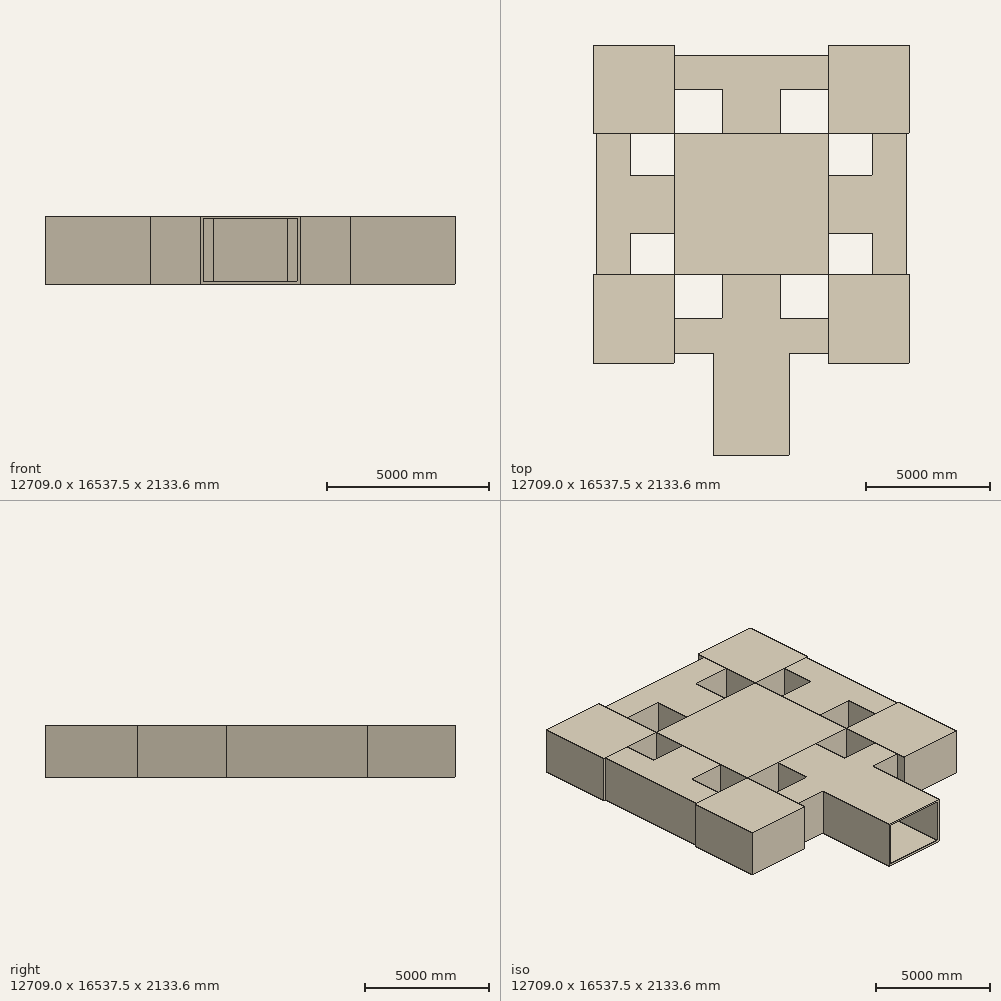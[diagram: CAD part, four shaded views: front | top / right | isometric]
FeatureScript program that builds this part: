
annotation { "Feature Type Name" : "Feature", "Feature Type Description" : "" }
export const myFeature = defineFeature(function(context is Context, id is Id, definition is map)
    precondition{}
    {
        {
            var Q0;
            Q0=qCreatedBy(makeId("Top.planeOp"),FACE);
            var sketch = newSketch(context, id + "F0", { "sketchPlane" : qUnion([Q0])});
            skLineSegment(sketch, "E0.top", {"start": v(13.99, 33.84) * mm, "end": v(36.85, 33.84) * mm});
            skLineSegment(sketch, "E0.right", {"start": v(36.85, 13.99) * mm, "end": v(36.85, 33.84) * mm});
            skLineSegment(sketch, "E1.bottom", {"start": v(36.85, 33.84) * mm, "end": v(56.25, 33.84) * mm});
            skLineSegment(sketch, "E1.top", {"start": v(36.85, 76.25) * mm, "end": v(75.65, 76.25) * mm});
            skLineSegment(sketch, "E1.left", {"start": v(36.85, 33.84) * mm, "end": v(36.85, 55.04) * mm});
            skLineSegment(sketch, "E1.right", {"start": v(75.65, 33.84) * mm, "end": v(75.65, 76.25) * mm});
            skLineSegment(sketch, "E2.bottom", {"start": v(36.85, 55.04) * mm, "end": v(13.99, 55.04) * mm});
            skLineSegment(sketch, "E2.top", {"start": v(36.85, 71.44) * mm, "end": v(0, 71.44) * mm});
            skLineSegment(sketch, "E3.trimOffspring", {"start": v(36.85, 71.44) * mm, "end": v(36.85, 76.25) * mm});
            skLineSegment(sketch, "E4.trimOffspring", {"start": v(56.25, 33.84) * mm, "end": v(58.05, 33.84) * mm});
            skLineSegment(sketch, "E5.right", {"start": v(13.99, 33.84) * mm, "end": v(13.99, 55.04) * mm});
            skLineSegment(sketch, "E6.left", {"start": v(36.85, 13.99) * mm, "end": v(58.05, 13.99) * mm});
            skLineSegment(sketch, "E7.top", {"start": v(74.45, 0) * mm, "end": v(74.45, 33.84) * mm});
            skLineSegment(sketch, "E8", {"start": v(58.05, 13.99) * mm, "end": v(58.05, 33.84) * mm});
            skLineSegment(sketch, "E9.MirrorCS", {"start": v(-36.85, 71.44) * mm, "end": v(-36.85, 76.25) * mm});
            skLineSegment(sketch, "E10.MirrorCS", {"start": v(-13.99, 33.84) * mm, "end": v(-36.85, 33.84) * mm});
            skLineSegment(sketch, "E11.MirrorCS", {"start": v(-36.85, 13.99) * mm, "end": v(-36.85, 33.84) * mm});
            skLineSegment(sketch, "E12.MirrorCS", {"start": v(-58.05, 13.99) * mm, "end": v(-58.05, 33.84) * mm});
            skLineSegment(sketch, "E13.MirrorCS", {"start": v(-74.45, 0) * mm, "end": v(-74.45, 33.84) * mm});
            skLineSegment(sketch, "E14.MirrorCS", {"start": v(-13.99, 33.84) * mm, "end": v(-13.99, 55.04) * mm});
            skLineSegment(sketch, "E15.MirrorCS", {"start": v(-56.25, 33.84) * mm, "end": v(-58.05, 33.84) * mm});
            skLineSegment(sketch, "E16.MirrorCS", {"start": v(-36.85, 33.84) * mm, "end": v(-56.25, 33.84) * mm});
            skLineSegment(sketch, "E17.MirrorCS", {"start": v(-36.85, 33.84) * mm, "end": v(-36.85, 55.04) * mm});
            skLineSegment(sketch, "E18.MirrorCS", {"start": v(-36.85, 76.25) * mm, "end": v(-75.65, 76.25) * mm});
            skLineSegment(sketch, "E19.MirrorCS", {"start": v(-36.85, 13.99) * mm, "end": v(-58.05, 13.99) * mm});
            skLineSegment(sketch, "E20.MirrorCS", {"start": v(-75.65, 33.84) * mm, "end": v(-75.65, 76.25) * mm});
            skLineSegment(sketch, "E21.MirrorCS", {"start": v(-36.85, 55.04) * mm, "end": v(-13.99, 55.04) * mm});
            skLineSegment(sketch, "E22.MirrorCS", {"start": v(-36.85, 71.44) * mm, "end": v(0, 71.44) * mm});
            skLineSegment(sketch, "E23.MirrorCS", {"start": v(-36.85, -71.44) * mm, "end": v(-36.85, -76.25) * mm});
            skLineSegment(sketch, "E24.MirrorCS", {"start": v(-36.85, -33.84) * mm, "end": v(-56.25, -33.84) * mm});
            skLineSegment(sketch, "E25.MirrorCS", {"start": v(36.85, -71.44) * mm, "end": v(36.85, -76.25) * mm});
            skLineSegment(sketch, "E26.MirrorCS", {"start": v(56.25, -33.84) * mm, "end": v(58.05, -33.84) * mm});
            skLineSegment(sketch, "E27.MirrorCS", {"start": v(-56.25, -33.84) * mm, "end": v(-58.05, -33.84) * mm});
            skLineSegment(sketch, "E28.MirrorCS", {"start": v(36.85, -71.44) * mm, "end": v(18.42, -71.44) * mm});
            skLineSegment(sketch, "E29.MirrorCS", {"start": v(36.85, -76.25) * mm, "end": v(75.65, -76.25) * mm});
            skLineSegment(sketch, "E30.MirrorCS", {"start": v(-13.99, -33.84) * mm, "end": v(-36.85, -33.84) * mm});
            skLineSegment(sketch, "E31.MirrorCS", {"start": v(-36.85, -13.99) * mm, "end": v(-36.85, -33.84) * mm});
            skLineSegment(sketch, "E32.MirrorCS", {"start": v(36.85, -55.04) * mm, "end": v(13.99, -55.04) * mm});
            skLineSegment(sketch, "E33.MirrorCS", {"start": v(-36.85, -13.99) * mm, "end": v(-58.05, -13.99) * mm});
            skLineSegment(sketch, "E34.MirrorCS", {"start": v(-36.85, -55.04) * mm, "end": v(-13.99, -55.04) * mm});
            skLineSegment(sketch, "E35.MirrorCS", {"start": v(-36.85, -33.84) * mm, "end": v(-36.85, -55.04) * mm});
            skLineSegment(sketch, "E36.MirrorCS", {"start": v(-36.85, -71.44) * mm, "end": v(-18.42, -71.44) * mm});
            skLineSegment(sketch, "E37.MirrorCS", {"start": v(36.85, -13.99) * mm, "end": v(36.85, -33.84) * mm});
            skLineSegment(sketch, "E38.MirrorCS", {"start": v(36.85, -13.99) * mm, "end": v(58.05, -13.99) * mm});
            skLineSegment(sketch, "E39.MirrorCS", {"start": v(36.85, -33.84) * mm, "end": v(56.25, -33.84) * mm});
            skLineSegment(sketch, "E40.MirrorCS", {"start": v(13.99, -33.84) * mm, "end": v(36.85, -33.84) * mm});
            skLineSegment(sketch, "E41.MirrorCS", {"start": v(58.05, -13.99) * mm, "end": v(58.05, -33.84) * mm});
            skLineSegment(sketch, "E42.MirrorCS", {"start": v(-74.45, 0) * mm, "end": v(-74.45, -33.84) * mm});
            skLineSegment(sketch, "E43.MirrorCS", {"start": v(-36.85, -76.25) * mm, "end": v(-75.65, -76.25) * mm});
            skLineSegment(sketch, "E44.MirrorCS", {"start": v(-58.05, -13.99) * mm, "end": v(-58.05, -33.84) * mm});
            skLineSegment(sketch, "E45.MirrorCS", {"start": v(13.99, -33.84) * mm, "end": v(13.99, -55.04) * mm});
            skLineSegment(sketch, "E46.MirrorCS", {"start": v(-13.99, -33.84) * mm, "end": v(-13.99, -55.04) * mm});
            skLineSegment(sketch, "E47.MirrorCS", {"start": v(75.65, -33.84) * mm, "end": v(75.65, -76.25) * mm});
            skLineSegment(sketch, "E48.MirrorCS", {"start": v(36.85, -33.84) * mm, "end": v(36.85, -55.04) * mm});
            skLineSegment(sketch, "E49.MirrorCS", {"start": v(74.45, 0) * mm, "end": v(74.45, -33.84) * mm});
            skLineSegment(sketch, "E50.MirrorCS", {"start": v(-75.65, -33.84) * mm, "end": v(-75.65, -76.25) * mm});
            skLineSegment(sketch, "E51.trimOffspring", {"start": v(-74.45, 33.84) * mm, "end": v(-75.65, 33.84) * mm});
            skLineSegment(sketch, "E52.trimOffspring", {"start": v(-74.45, -33.84) * mm, "end": v(-75.65, -33.84) * mm});
            skLineSegment(sketch, "E53.trimOffspring", {"start": v(74.45, -33.84) * mm, "end": v(75.65, -33.84) * mm});
            skLineSegment(sketch, "E54.trimOffspring", {"start": v(74.45, 33.84) * mm, "end": v(75.65, 33.84) * mm});
            skPoint(sketch, "E55.oppositeSnap0", {"position": v(18.42, -71.44) * mm});
            skLineSegment(sketch, "E55.top", {"start": v(-18.42, -120.63) * mm, "end": v(18.42, -120.63) * mm});
            skLineSegment(sketch, "E55.left", {"start": v(-18.42, -71.44) * mm, "end": v(-18.42, -120.63) * mm});
            skLineSegment(sketch, "E55.right", {"start": v(18.42, -71.44) * mm, "end": v(18.42, -120.63) * mm});
            skPoint(sketch, "E56.orphan", {"position": v(0, -71.44) * mm});
            skLineSegment(sketch, "E57", {"start": v(-13.99, 33.84) * mm, "end": v(13.99, 33.84) * mm});
            skLineSegment(sketch, "E58", {"start": v(36.85, 55.04) * mm, "end": v(36.85, 71.44) * mm});
            skLineSegment(sketch, "E59", {"start": v(-36.85, 71.44) * mm, "end": v(-36.85, 55.04) * mm});
            skLineSegment(sketch, "E60", {"start": v(13.99, -33.84) * mm, "end": v(-13.99, -33.84) * mm});
            skLineSegment(sketch, "E61", {"start": v(-36.85, -55.04) * mm, "end": v(-36.85, -71.44) * mm});
            skLineSegment(sketch, "E62", {"start": v(36.85, -71.44) * mm, "end": v(36.85, -55.04) * mm});
            skLineSegment(sketch, "E63", {"start": v(58.05, -33.83) * mm, "end": v(74.45, -33.83) * mm});
            skLineSegment(sketch, "E64", {"start": v(74.45, 33.84) * mm, "end": v(58.05, 33.84) * mm});
            skLineSegment(sketch, "E65", {"start": v(36.85, 13.99) * mm, "end": v(36.85, -13.99) * mm});
            skLineSegment(sketch, "E66", {"start": v(-36.85, 13.99) * mm, "end": v(-36.85, -13.99) * mm});
            skLineSegment(sketch, "E67", {"start": v(-58.05, -33.84) * mm, "end": v(-74.45, -33.84) * mm});
            skLineSegment(sketch, "E68", {"start": v(-74.45, 33.84) * mm, "end": v(-58.05, 33.84) * mm});
            skSolve(sketch);
        }
        {
            var Q0;
            Q0=makeQuery(id+"F0.imprint","IMPRINT",FACE,{"disambiguationData":[TD([[makeQuery(id+"F0.imprint","IMPRINT",EDGE,{"derivedFrom":sQuery(id+"F0.wireOp",EDGE,"E0.top")}),-1.0]])]});
            var Q1;
            Q1=makeQuery(id+"F0.imprint","IMPRINT",FACE,{"disambiguationData":[TD([[makeQuery(id+"F0.imprint","IMPRINT",EDGE,{"derivedFrom":sQuery(id+"F0.wireOp",EDGE,"E9.MirrorCS")}),1.0]])]});
            var Q2;
            Q2=makeQuery(id+"F0.imprint","IMPRINT",FACE,{"disambiguationData":[TD([[makeQuery(id+"F0.imprint","IMPRINT",EDGE,{"derivedFrom":sQuery(id+"F0.wireOp",EDGE,"E1.bottom")}),1.0]])]});
            var Q3;
            Q3=makeQuery(id+"F0.imprint","IMPRINT",FACE,{"disambiguationData":[TD([[makeQuery(id+"F0.imprint","IMPRINT",EDGE,{"derivedFrom":sQuery(id+"F0.wireOp",EDGE,"E25.MirrorCS")}),1.0]])]});
            var Q4;
            Q4=makeQuery(id+"F0.imprint","IMPRINT",FACE,{"disambiguationData":[TD([[makeQuery(id+"F0.imprint","IMPRINT",EDGE,{"derivedFrom":sQuery(id+"F0.wireOp",EDGE,"E23.MirrorCS")}),-1.0]])]});
            extrude(context, id + "F1", {"entities" : qUnion([Q0, Q1, Q2, Q3, Q4]), "depth" : 25.4 * mm, "offsetDistance" : 25.4 * mm});
        }
        {
            var Q0;
            Q0=makeQuery(id+"F0.imprint","IMPRINT",FACE,{"disambiguationData":[TD([[makeQuery(id+"F0.imprint","IMPRINT",EDGE,{"derivedFrom":sQuery(id+"F0.wireOp",EDGE,"E28.MirrorCS")}),-1.0]])]});
            var Q1;
            Q1=makeQuery(id+"F0.imprint","IMPRINT",FACE,{"disambiguationData":[TD([[makeQuery(id+"F0.imprint","IMPRINT",EDGE,{"derivedFrom":sQuery(id+"F0.wireOp",EDGE,"E6.left")}),-1.0]])]});
            var Q2;
            Q2=makeQuery(id+"F0.imprint","IMPRINT",FACE,{"disambiguationData":[TD([[makeQuery(id+"F0.imprint","IMPRINT",EDGE,{"derivedFrom":sQuery(id+"F0.wireOp",EDGE,"E2.bottom")}),-1.0]])]});
            var Q3;
            Q3=makeQuery(id+"F0.imprint","IMPRINT",FACE,{"disambiguationData":[TD([[makeQuery(id+"F0.imprint","IMPRINT",EDGE,{"derivedFrom":sQuery(id+"F0.wireOp",EDGE,"E12.MirrorCS")}),1.0]])]});
            extrude(context, id + "F2", {"entities" : qUnion([Q0, Q1, Q2, Q3]), "depth" : 25.4 * mm, "offsetDistance" : 25.4 * mm});
        }
        {
            var Q0;
            Q0=makeQuery(id+"F1.opExtrude","SWEPT_BODY",BODY,{"disambiguationData":[OSD([sQuery(id+"F0.wireOp",EDGE,"E25.MirrorCS"),sQuery(id+"F0.wireOp",EDGE,"E26.MirrorCS"),sQuery(id+"F0.wireOp",EDGE,"E29.MirrorCS"),sQuery(id+"F0.wireOp",EDGE,"E39.MirrorCS"),sQuery(id+"F0.wireOp",EDGE,"E41.MirrorCS"),sQuery(id+"F0.wireOp",EDGE,"E47.MirrorCS"),sQuery(id+"F0.wireOp",EDGE,"E48.MirrorCS"),sQuery(id+"F0.wireOp",EDGE,"E49.MirrorCS"),sQuery(id+"F0.wireOp",EDGE,"E53.trimOffspring"),sQuery(id+"F0.wireOp",EDGE,"E62"),sQuery(id+"F0.wireOp",EDGE,"E63")])]});
            var Q1;
            Q1=makeQuery(id+"F1.opExtrude","SWEPT_BODY",BODY,{"disambiguationData":[OSD([sQuery(id+"F0.wireOp",EDGE,"E23.MirrorCS"),sQuery(id+"F0.wireOp",EDGE,"E24.MirrorCS"),sQuery(id+"F0.wireOp",EDGE,"E27.MirrorCS"),sQuery(id+"F0.wireOp",EDGE,"E35.MirrorCS"),sQuery(id+"F0.wireOp",EDGE,"E43.MirrorCS"),sQuery(id+"F0.wireOp",EDGE,"E50.MirrorCS"),sQuery(id+"F0.wireOp",EDGE,"E52.trimOffspring"),sQuery(id+"F0.wireOp",EDGE,"E61"),sQuery(id+"F0.wireOp",EDGE,"E67")])]});
            var Q2;
            Q2=makeQuery(id+"F1.opExtrude","SWEPT_BODY",BODY,{"disambiguationData":[OSD([sQuery(id+"F0.wireOp",EDGE,"E1.bottom"),sQuery(id+"F0.wireOp",EDGE,"E1.top"),sQuery(id+"F0.wireOp",EDGE,"E1.left"),sQuery(id+"F0.wireOp",EDGE,"E1.right"),sQuery(id+"F0.wireOp",EDGE,"E3.trimOffspring"),sQuery(id+"F0.wireOp",EDGE,"E4.trimOffspring"),sQuery(id+"F0.wireOp",EDGE,"E54.trimOffspring"),sQuery(id+"F0.wireOp",EDGE,"E58"),sQuery(id+"F0.wireOp",EDGE,"E64")])]});
            var Q3;
            Q3=makeQuery(id+"F1.opExtrude","SWEPT_BODY",BODY,{"disambiguationData":[OSD([sQuery(id+"F0.wireOp",EDGE,"E9.MirrorCS"),sQuery(id+"F0.wireOp",EDGE,"E15.MirrorCS"),sQuery(id+"F0.wireOp",EDGE,"E16.MirrorCS"),sQuery(id+"F0.wireOp",EDGE,"E17.MirrorCS"),sQuery(id+"F0.wireOp",EDGE,"E18.MirrorCS"),sQuery(id+"F0.wireOp",EDGE,"E20.MirrorCS"),sQuery(id+"F0.wireOp",EDGE,"E51.trimOffspring"),sQuery(id+"F0.wireOp",EDGE,"E59"),sQuery(id+"F0.wireOp",EDGE,"E68")])]});
            var Q4;
            Q4=makeQuery(id+"F1.opExtrude","SWEPT_BODY",BODY,{"disambiguationData":[OSD([sQuery(id+"F0.wireOp",EDGE,"E0.top"),sQuery(id+"F0.wireOp",EDGE,"E0.right"),sQuery(id+"F0.wireOp",EDGE,"E10.MirrorCS"),sQuery(id+"F0.wireOp",EDGE,"E11.MirrorCS"),sQuery(id+"F0.wireOp",EDGE,"E30.MirrorCS"),sQuery(id+"F0.wireOp",EDGE,"E31.MirrorCS"),sQuery(id+"F0.wireOp",EDGE,"E37.MirrorCS"),sQuery(id+"F0.wireOp",EDGE,"E40.MirrorCS"),sQuery(id+"F0.wireOp",EDGE,"E57"),sQuery(id+"F0.wireOp",EDGE,"E60"),sQuery(id+"F0.wireOp",EDGE,"E65"),sQuery(id+"F0.wireOp",EDGE,"E66")])]});
            var Q5;
            Q5=makeQuery(id+"F2.opExtrude","SWEPT_BODY",BODY,{"disambiguationData":[OSD([sQuery(id+"F0.wireOp",EDGE,"E2.bottom"),sQuery(id+"F0.wireOp",EDGE,"E2.top"),sQuery(id+"F0.wireOp",EDGE,"E5.right"),sQuery(id+"F0.wireOp",EDGE,"E14.MirrorCS"),sQuery(id+"F0.wireOp",EDGE,"E21.MirrorCS"),sQuery(id+"F0.wireOp",EDGE,"E22.MirrorCS"),sQuery(id+"F0.wireOp",EDGE,"E57"),sQuery(id+"F0.wireOp",EDGE,"E58"),sQuery(id+"F0.wireOp",EDGE,"E59")])]});
            var Q6;
            Q6=makeQuery(id+"F2.opExtrude","SWEPT_BODY",BODY,{"disambiguationData":[OSD([sQuery(id+"F0.wireOp",EDGE,"E6.left"),sQuery(id+"F0.wireOp",EDGE,"E7.top"),sQuery(id+"F0.wireOp",EDGE,"E8"),sQuery(id+"F0.wireOp",EDGE,"E38.MirrorCS"),sQuery(id+"F0.wireOp",EDGE,"E41.MirrorCS"),sQuery(id+"F0.wireOp",EDGE,"E49.MirrorCS"),sQuery(id+"F0.wireOp",EDGE,"E63"),sQuery(id+"F0.wireOp",EDGE,"E64"),sQuery(id+"F0.wireOp",EDGE,"E65")])]});
            var Q7;
            Q7=makeQuery(id+"F2.opExtrude","SWEPT_BODY",BODY,{"disambiguationData":[OSD([sQuery(id+"F0.wireOp",EDGE,"E12.MirrorCS"),sQuery(id+"F0.wireOp",EDGE,"E13.MirrorCS"),sQuery(id+"F0.wireOp",EDGE,"E19.MirrorCS"),sQuery(id+"F0.wireOp",EDGE,"E33.MirrorCS"),sQuery(id+"F0.wireOp",EDGE,"E42.MirrorCS"),sQuery(id+"F0.wireOp",EDGE,"E44.MirrorCS"),sQuery(id+"F0.wireOp",EDGE,"E66"),sQuery(id+"F0.wireOp",EDGE,"E67"),sQuery(id+"F0.wireOp",EDGE,"E68")])]});
            var Q8;
            Q8=makeQuery(id+"F2.opExtrude","SWEPT_BODY",BODY,{"disambiguationData":[OSD([sQuery(id+"F0.wireOp",EDGE,"E28.MirrorCS"),sQuery(id+"F0.wireOp",EDGE,"E32.MirrorCS"),sQuery(id+"F0.wireOp",EDGE,"E34.MirrorCS"),sQuery(id+"F0.wireOp",EDGE,"E36.MirrorCS"),sQuery(id+"F0.wireOp",EDGE,"E45.MirrorCS"),sQuery(id+"F0.wireOp",EDGE,"E46.MirrorCS"),sQuery(id+"F0.wireOp",EDGE,"E55.top"),sQuery(id+"F0.wireOp",EDGE,"E55.left"),sQuery(id+"F0.wireOp",EDGE,"E55.right"),sQuery(id+"F0.wireOp",EDGE,"E60"),sQuery(id+"F0.wireOp",EDGE,"E61"),sQuery(id+"F0.wireOp",EDGE,"E62")])]});
            var Q9;
            Q9=qCreatedBy(makeId("Origin.pointOp"),VERTEX);
            transform(context, id + "F3", {"entities" : qUnion([Q0, Q1, Q2, Q3, Q4, Q5, Q6, Q7, Q8]), "transformType" : TransformType.SCALE_UNIFORMLY, "scale" : 84, "scalePoint" : qUnion([Q9]), "makeCopy" : false});
        }
        {
            var Q0;
            Q0=makeQuery(id+"F1.opExtrude","CAP_FACE",FACE,{"disambiguationData":[OSD([sQuery(id+"F0.wireOp",EDGE,"E25.MirrorCS"),sQuery(id+"F0.wireOp",EDGE,"E26.MirrorCS"),sQuery(id+"F0.wireOp",EDGE,"E29.MirrorCS"),sQuery(id+"F0.wireOp",EDGE,"E39.MirrorCS"),sQuery(id+"F0.wireOp",EDGE,"E41.MirrorCS"),sQuery(id+"F0.wireOp",EDGE,"E47.MirrorCS"),sQuery(id+"F0.wireOp",EDGE,"E48.MirrorCS"),sQuery(id+"F0.wireOp",EDGE,"E49.MirrorCS"),sQuery(id+"F0.wireOp",EDGE,"E53.trimOffspring"),sQuery(id+"F0.wireOp",EDGE,"E62"),sQuery(id+"F0.wireOp",EDGE,"E63")])],"isStart":true});
            var Q1;
            Q1=makeQuery(id+"F1.opExtrude","CAP_FACE",FACE,{"disambiguationData":[OSD([sQuery(id+"F0.wireOp",EDGE,"E25.MirrorCS"),sQuery(id+"F0.wireOp",EDGE,"E26.MirrorCS"),sQuery(id+"F0.wireOp",EDGE,"E29.MirrorCS"),sQuery(id+"F0.wireOp",EDGE,"E39.MirrorCS"),sQuery(id+"F0.wireOp",EDGE,"E41.MirrorCS"),sQuery(id+"F0.wireOp",EDGE,"E47.MirrorCS"),sQuery(id+"F0.wireOp",EDGE,"E48.MirrorCS"),sQuery(id+"F0.wireOp",EDGE,"E49.MirrorCS"),sQuery(id+"F0.wireOp",EDGE,"E53.trimOffspring"),sQuery(id+"F0.wireOp",EDGE,"E62"),sQuery(id+"F0.wireOp",EDGE,"E63")])],"isStart":false});
            var Q2;
            Q2=makeQuery(id+"F1.opExtrude","SWEPT_FACE",FACE,{"disambiguationData":[OSD([sQuery(id+"F0.wireOp",EDGE,"E53.trimOffspring")])]});
            var Q3;
            Q3=makeQuery(id+"F1.opExtrude","SWEPT_FACE",FACE,{"disambiguationData":[OSD([sQuery(id+"F0.wireOp",EDGE,"E47.MirrorCS")])]});
            var Q4;
            Q4=makeQuery(id+"F1.opExtrude","SWEPT_FACE",FACE,{"disambiguationData":[OSD([sQuery(id+"F0.wireOp",EDGE,"E26.MirrorCS"),sQuery(id+"F0.wireOp",EDGE,"E39.MirrorCS")])]});
            var Q5;
            Q5=makeQuery(id+"F1.opExtrude","SWEPT_FACE",FACE,{"disambiguationData":[OSD([sQuery(id+"F0.wireOp",EDGE,"E29.MirrorCS")])]});
            var Q6;
            Q6=makeQuery(id+"F1.opExtrude","SWEPT_FACE",FACE,{"disambiguationData":[OSD([sQuery(id+"F0.wireOp",EDGE,"E50.MirrorCS")])]});
            var Q7;
            Q7=makeQuery(id+"F1.opExtrude","CAP_FACE",FACE,{"disambiguationData":[OSD([sQuery(id+"F0.wireOp",EDGE,"E23.MirrorCS"),sQuery(id+"F0.wireOp",EDGE,"E24.MirrorCS"),sQuery(id+"F0.wireOp",EDGE,"E27.MirrorCS"),sQuery(id+"F0.wireOp",EDGE,"E35.MirrorCS"),sQuery(id+"F0.wireOp",EDGE,"E43.MirrorCS"),sQuery(id+"F0.wireOp",EDGE,"E50.MirrorCS"),sQuery(id+"F0.wireOp",EDGE,"E52.trimOffspring"),sQuery(id+"F0.wireOp",EDGE,"E61"),sQuery(id+"F0.wireOp",EDGE,"E67")])],"isStart":false});
            var Q8;
            Q8=makeQuery(id+"F1.opExtrude","SWEPT_FACE",FACE,{"disambiguationData":[OSD([sQuery(id+"F0.wireOp",EDGE,"E23.MirrorCS"),sQuery(id+"F0.wireOp",EDGE,"E35.MirrorCS"),sQuery(id+"F0.wireOp",EDGE,"E61")])]});
            var Q9;
            Q9=makeQuery(id+"F1.opExtrude","SWEPT_FACE",FACE,{"disambiguationData":[OSD([sQuery(id+"F0.wireOp",EDGE,"E24.MirrorCS"),sQuery(id+"F0.wireOp",EDGE,"E27.MirrorCS"),sQuery(id+"F0.wireOp",EDGE,"E52.trimOffspring"),sQuery(id+"F0.wireOp",EDGE,"E67")])]});
            var Q10;
            Q10=makeQuery(id+"F1.opExtrude","SWEPT_FACE",FACE,{"disambiguationData":[OSD([sQuery(id+"F0.wireOp",EDGE,"E43.MirrorCS")])]});
            var Q11;
            Q11=makeQuery(id+"F1.opExtrude","SWEPT_FACE",FACE,{"disambiguationData":[OSD([sQuery(id+"F0.wireOp",EDGE,"E1.right")])]});
            var Q12;
            Q12=makeQuery(id+"F1.opExtrude","CAP_FACE",FACE,{"disambiguationData":[OSD([sQuery(id+"F0.wireOp",EDGE,"E1.bottom"),sQuery(id+"F0.wireOp",EDGE,"E1.top"),sQuery(id+"F0.wireOp",EDGE,"E1.left"),sQuery(id+"F0.wireOp",EDGE,"E1.right"),sQuery(id+"F0.wireOp",EDGE,"E3.trimOffspring"),sQuery(id+"F0.wireOp",EDGE,"E4.trimOffspring"),sQuery(id+"F0.wireOp",EDGE,"E54.trimOffspring"),sQuery(id+"F0.wireOp",EDGE,"E58"),sQuery(id+"F0.wireOp",EDGE,"E64")])],"isStart":false});
            var Q13;
            Q13=makeQuery(id+"F1.opExtrude","SWEPT_FACE",FACE,{"disambiguationData":[OSD([sQuery(id+"F0.wireOp",EDGE,"E1.left"),sQuery(id+"F0.wireOp",EDGE,"E3.trimOffspring"),sQuery(id+"F0.wireOp",EDGE,"E58")])]});
            var Q14;
            Q14=makeQuery(id+"F1.opExtrude","SWEPT_FACE",FACE,{"disambiguationData":[OSD([sQuery(id+"F0.wireOp",EDGE,"E1.bottom"),sQuery(id+"F0.wireOp",EDGE,"E4.trimOffspring"),sQuery(id+"F0.wireOp",EDGE,"E54.trimOffspring"),sQuery(id+"F0.wireOp",EDGE,"E64")])]});
            var Q15;
            Q15=makeQuery(id+"F1.opExtrude","CAP_FACE",FACE,{"disambiguationData":[OSD([sQuery(id+"F0.wireOp",EDGE,"E9.MirrorCS"),sQuery(id+"F0.wireOp",EDGE,"E15.MirrorCS"),sQuery(id+"F0.wireOp",EDGE,"E16.MirrorCS"),sQuery(id+"F0.wireOp",EDGE,"E17.MirrorCS"),sQuery(id+"F0.wireOp",EDGE,"E18.MirrorCS"),sQuery(id+"F0.wireOp",EDGE,"E20.MirrorCS"),sQuery(id+"F0.wireOp",EDGE,"E51.trimOffspring"),sQuery(id+"F0.wireOp",EDGE,"E59"),sQuery(id+"F0.wireOp",EDGE,"E68")])],"isStart":false});
            var Q16;
            Q16=makeQuery(id+"F1.opExtrude","SWEPT_FACE",FACE,{"disambiguationData":[OSD([sQuery(id+"F0.wireOp",EDGE,"E9.MirrorCS"),sQuery(id+"F0.wireOp",EDGE,"E17.MirrorCS"),sQuery(id+"F0.wireOp",EDGE,"E59")])]});
            var Q17;
            Q17=makeQuery(id+"F1.opExtrude","SWEPT_FACE",FACE,{"disambiguationData":[OSD([sQuery(id+"F0.wireOp",EDGE,"E15.MirrorCS"),sQuery(id+"F0.wireOp",EDGE,"E16.MirrorCS"),sQuery(id+"F0.wireOp",EDGE,"E51.trimOffspring"),sQuery(id+"F0.wireOp",EDGE,"E68")])]});
            var Q18;
            Q18=makeQuery(id+"F1.opExtrude","SWEPT_FACE",FACE,{"disambiguationData":[OSD([sQuery(id+"F0.wireOp",EDGE,"E20.MirrorCS")])]});
            var Q19;
            Q19=makeQuery(id+"F1.opExtrude","SWEPT_FACE",FACE,{"disambiguationData":[OSD([sQuery(id+"F0.wireOp",EDGE,"E18.MirrorCS")])]});
            var Q20;
            Q20=makeQuery(id+"F1.opExtrude","CAP_FACE",FACE,{"disambiguationData":[OSD([sQuery(id+"F0.wireOp",EDGE,"E0.top"),sQuery(id+"F0.wireOp",EDGE,"E0.right"),sQuery(id+"F0.wireOp",EDGE,"E10.MirrorCS"),sQuery(id+"F0.wireOp",EDGE,"E11.MirrorCS"),sQuery(id+"F0.wireOp",EDGE,"E30.MirrorCS"),sQuery(id+"F0.wireOp",EDGE,"E31.MirrorCS"),sQuery(id+"F0.wireOp",EDGE,"E37.MirrorCS"),sQuery(id+"F0.wireOp",EDGE,"E40.MirrorCS"),sQuery(id+"F0.wireOp",EDGE,"E57"),sQuery(id+"F0.wireOp",EDGE,"E60"),sQuery(id+"F0.wireOp",EDGE,"E65"),sQuery(id+"F0.wireOp",EDGE,"E66")])],"isStart":false});
            var Q21;
            Q21=makeQuery(id+"F1.opExtrude","SWEPT_FACE",FACE,{"disambiguationData":[OSD([sQuery(id+"F0.wireOp",EDGE,"E11.MirrorCS"),sQuery(id+"F0.wireOp",EDGE,"E31.MirrorCS"),sQuery(id+"F0.wireOp",EDGE,"E66")])]});
            var Q22;
            Q22=makeQuery(id+"F1.opExtrude","SWEPT_FACE",FACE,{"disambiguationData":[OSD([sQuery(id+"F0.wireOp",EDGE,"E0.top"),sQuery(id+"F0.wireOp",EDGE,"E10.MirrorCS"),sQuery(id+"F0.wireOp",EDGE,"E57")])]});
            var Q23;
            Q23=makeQuery(id+"F1.opExtrude","SWEPT_FACE",FACE,{"disambiguationData":[OSD([sQuery(id+"F0.wireOp",EDGE,"E30.MirrorCS"),sQuery(id+"F0.wireOp",EDGE,"E40.MirrorCS"),sQuery(id+"F0.wireOp",EDGE,"E60")])]});
            var Q24;
            Q24=makeQuery(id+"F1.opExtrude","SWEPT_FACE",FACE,{"disambiguationData":[OSD([sQuery(id+"F0.wireOp",EDGE,"E0.right"),sQuery(id+"F0.wireOp",EDGE,"E37.MirrorCS"),sQuery(id+"F0.wireOp",EDGE,"E65")])]});
            var Q25;
            Q25=makeQuery(id+"F2.opExtrude","SWEPT_FACE",FACE,{"disambiguationData":[OSD([sQuery(id+"F0.wireOp",EDGE,"E14.MirrorCS")])]});
            var Q26;
            Q26=makeQuery(id+"F2.opExtrude","SWEPT_FACE",FACE,{"disambiguationData":[OSD([sQuery(id+"F0.wireOp",EDGE,"E21.MirrorCS")])]});
            var Q27;
            Q27=makeQuery(id+"F2.opExtrude","SWEPT_FACE",FACE,{"disambiguationData":[OSD([sQuery(id+"F0.wireOp",EDGE,"E5.right")])]});
            var Q28;
            Q28=makeQuery(id+"F2.opExtrude","CAP_FACE",FACE,{"disambiguationData":[OSD([sQuery(id+"F0.wireOp",EDGE,"E2.bottom"),sQuery(id+"F0.wireOp",EDGE,"E2.top"),sQuery(id+"F0.wireOp",EDGE,"E5.right"),sQuery(id+"F0.wireOp",EDGE,"E14.MirrorCS"),sQuery(id+"F0.wireOp",EDGE,"E21.MirrorCS"),sQuery(id+"F0.wireOp",EDGE,"E22.MirrorCS"),sQuery(id+"F0.wireOp",EDGE,"E57"),sQuery(id+"F0.wireOp",EDGE,"E58"),sQuery(id+"F0.wireOp",EDGE,"E59")])],"isStart":false});
            var Q29;
            Q29=makeQuery(id+"F2.opExtrude","SWEPT_FACE",FACE,{"disambiguationData":[OSD([sQuery(id+"F0.wireOp",EDGE,"E2.bottom")])]});
            var Q30;
            Q30=makeQuery(id+"F2.opExtrude","CAP_FACE",FACE,{"disambiguationData":[OSD([sQuery(id+"F0.wireOp",EDGE,"E6.left"),sQuery(id+"F0.wireOp",EDGE,"E7.top"),sQuery(id+"F0.wireOp",EDGE,"E8"),sQuery(id+"F0.wireOp",EDGE,"E38.MirrorCS"),sQuery(id+"F0.wireOp",EDGE,"E41.MirrorCS"),sQuery(id+"F0.wireOp",EDGE,"E49.MirrorCS"),sQuery(id+"F0.wireOp",EDGE,"E63"),sQuery(id+"F0.wireOp",EDGE,"E64"),sQuery(id+"F0.wireOp",EDGE,"E65")])],"isStart":true});
            var Q31;
            Q31=makeQuery(id+"F2.opExtrude","SWEPT_FACE",FACE,{"disambiguationData":[OSD([sQuery(id+"F0.wireOp",EDGE,"E41.MirrorCS")])]});
            var Q32;
            Q32=makeQuery(id+"F2.opExtrude","SWEPT_FACE",FACE,{"disambiguationData":[OSD([sQuery(id+"F0.wireOp",EDGE,"E38.MirrorCS")])]});
            var Q33;
            Q33=makeQuery(id+"F2.opExtrude","CAP_FACE",FACE,{"disambiguationData":[OSD([sQuery(id+"F0.wireOp",EDGE,"E6.left"),sQuery(id+"F0.wireOp",EDGE,"E7.top"),sQuery(id+"F0.wireOp",EDGE,"E8"),sQuery(id+"F0.wireOp",EDGE,"E38.MirrorCS"),sQuery(id+"F0.wireOp",EDGE,"E41.MirrorCS"),sQuery(id+"F0.wireOp",EDGE,"E49.MirrorCS"),sQuery(id+"F0.wireOp",EDGE,"E63"),sQuery(id+"F0.wireOp",EDGE,"E64"),sQuery(id+"F0.wireOp",EDGE,"E65")])],"isStart":false});
            var Q34;
            Q34=makeQuery(id+"F2.opExtrude","SWEPT_FACE",FACE,{"disambiguationData":[OSD([sQuery(id+"F0.wireOp",EDGE,"E8")])]});
            var Q35;
            Q35=makeQuery(id+"F2.opExtrude","SWEPT_FACE",FACE,{"disambiguationData":[OSD([sQuery(id+"F0.wireOp",EDGE,"E65")])]});
            var Q36;
            Q36=makeQuery(id+"F2.opExtrude","SWEPT_FACE",FACE,{"disambiguationData":[OSD([sQuery(id+"F0.wireOp",EDGE,"E6.left")])]});
            var Q37;
            Q37=makeQuery(id+"F2.opExtrude","SWEPT_FACE",FACE,{"disambiguationData":[OSD([sQuery(id+"F0.wireOp",EDGE,"E7.top"),sQuery(id+"F0.wireOp",EDGE,"E49.MirrorCS")])]});
            var Q38;
            Q38=makeQuery(id+"F2.opExtrude","SWEPT_FACE",FACE,{"disambiguationData":[OSD([sQuery(id+"F0.wireOp",EDGE,"E13.MirrorCS"),sQuery(id+"F0.wireOp",EDGE,"E42.MirrorCS")])]});
            var Q39;
            Q39=makeQuery(id+"F2.opExtrude","SWEPT_FACE",FACE,{"disambiguationData":[OSD([sQuery(id+"F0.wireOp",EDGE,"E33.MirrorCS")])]});
            var Q40;
            Q40=makeQuery(id+"F2.opExtrude","SWEPT_FACE",FACE,{"disambiguationData":[OSD([sQuery(id+"F0.wireOp",EDGE,"E12.MirrorCS")])]});
            var Q41;
            Q41=makeQuery(id+"F2.opExtrude","SWEPT_FACE",FACE,{"disambiguationData":[OSD([sQuery(id+"F0.wireOp",EDGE,"E44.MirrorCS")])]});
            var Q42;
            Q42=makeQuery(id+"F2.opExtrude","SWEPT_FACE",FACE,{"disambiguationData":[OSD([sQuery(id+"F0.wireOp",EDGE,"E19.MirrorCS")])]});
            var Q43;
            Q43=makeQuery(id+"F2.opExtrude","CAP_FACE",FACE,{"disambiguationData":[OSD([sQuery(id+"F0.wireOp",EDGE,"E12.MirrorCS"),sQuery(id+"F0.wireOp",EDGE,"E13.MirrorCS"),sQuery(id+"F0.wireOp",EDGE,"E19.MirrorCS"),sQuery(id+"F0.wireOp",EDGE,"E33.MirrorCS"),sQuery(id+"F0.wireOp",EDGE,"E42.MirrorCS"),sQuery(id+"F0.wireOp",EDGE,"E44.MirrorCS"),sQuery(id+"F0.wireOp",EDGE,"E66"),sQuery(id+"F0.wireOp",EDGE,"E67"),sQuery(id+"F0.wireOp",EDGE,"E68")])],"isStart":false});
            var Q44;
            Q44=makeQuery(id+"F2.opExtrude","SWEPT_FACE",FACE,{"disambiguationData":[OSD([sQuery(id+"F0.wireOp",EDGE,"E36.MirrorCS")])]});
            var Q45;
            Q45=makeQuery(id+"F2.opExtrude","SWEPT_FACE",FACE,{"disambiguationData":[OSD([sQuery(id+"F0.wireOp",EDGE,"E61")])]});
            var Q46;
            Q46=makeQuery(id+"F2.opExtrude","SWEPT_FACE",FACE,{"disambiguationData":[OSD([sQuery(id+"F0.wireOp",EDGE,"E55.top")])]});
            var Q47;
            Q47=makeQuery(id+"F2.opExtrude","SWEPT_FACE",FACE,{"disambiguationData":[OSD([sQuery(id+"F0.wireOp",EDGE,"E55.left")])]});
            var Q48;
            Q48=makeQuery(id+"F2.opExtrude","SWEPT_FACE",FACE,{"disambiguationData":[OSD([sQuery(id+"F0.wireOp",EDGE,"E55.right")])]});
            var Q49;
            Q49=makeQuery(id+"F2.opExtrude","SWEPT_FACE",FACE,{"disambiguationData":[OSD([sQuery(id+"F0.wireOp",EDGE,"E28.MirrorCS")])]});
            var Q50;
            Q50=makeQuery(id+"F2.opExtrude","SWEPT_FACE",FACE,{"disambiguationData":[OSD([sQuery(id+"F0.wireOp",EDGE,"E34.MirrorCS")])]});
            var Q51;
            Q51=makeQuery(id+"F2.opExtrude","SWEPT_FACE",FACE,{"disambiguationData":[OSD([sQuery(id+"F0.wireOp",EDGE,"E32.MirrorCS")])]});
            var Q52;
            Q52=makeQuery(id+"F2.opExtrude","CAP_FACE",FACE,{"disambiguationData":[OSD([sQuery(id+"F0.wireOp",EDGE,"E28.MirrorCS"),sQuery(id+"F0.wireOp",EDGE,"E32.MirrorCS"),sQuery(id+"F0.wireOp",EDGE,"E34.MirrorCS"),sQuery(id+"F0.wireOp",EDGE,"E36.MirrorCS"),sQuery(id+"F0.wireOp",EDGE,"E45.MirrorCS"),sQuery(id+"F0.wireOp",EDGE,"E46.MirrorCS"),sQuery(id+"F0.wireOp",EDGE,"E55.top"),sQuery(id+"F0.wireOp",EDGE,"E55.left"),sQuery(id+"F0.wireOp",EDGE,"E55.right"),sQuery(id+"F0.wireOp",EDGE,"E60"),sQuery(id+"F0.wireOp",EDGE,"E61"),sQuery(id+"F0.wireOp",EDGE,"E62")])],"isStart":false});
            var Q53;
            Q53=makeQuery(id+"F2.opExtrude","SWEPT_FACE",FACE,{"disambiguationData":[OSD([sQuery(id+"F0.wireOp",EDGE,"E46.MirrorCS")])]});
            var Q54;
            Q54=makeQuery(id+"F1.opExtrude","SWEPT_FACE",FACE,{"disambiguationData":[OSD([sQuery(id+"F0.wireOp",EDGE,"E25.MirrorCS"),sQuery(id+"F0.wireOp",EDGE,"E48.MirrorCS"),sQuery(id+"F0.wireOp",EDGE,"E62")])]});
            var Q55;
            Q55=makeQuery(id+"F1.opExtrude","SWEPT_FACE",FACE,{"disambiguationData":[OSD([sQuery(id+"F0.wireOp",EDGE,"E63")])]});
            var Q56;
            Q56=makeQuery(id+"F1.opExtrude","SWEPT_FACE",FACE,{"disambiguationData":[OSD([sQuery(id+"F0.wireOp",EDGE,"E41.MirrorCS")])]});
            var Q57;
            Q57=makeQuery(id+"F1.opExtrude","CAP_FACE",FACE,{"disambiguationData":[OSD([sQuery(id+"F0.wireOp",EDGE,"E23.MirrorCS"),sQuery(id+"F0.wireOp",EDGE,"E24.MirrorCS"),sQuery(id+"F0.wireOp",EDGE,"E27.MirrorCS"),sQuery(id+"F0.wireOp",EDGE,"E35.MirrorCS"),sQuery(id+"F0.wireOp",EDGE,"E43.MirrorCS"),sQuery(id+"F0.wireOp",EDGE,"E50.MirrorCS"),sQuery(id+"F0.wireOp",EDGE,"E52.trimOffspring"),sQuery(id+"F0.wireOp",EDGE,"E61"),sQuery(id+"F0.wireOp",EDGE,"E67")])],"isStart":true});
            var Q58;
            Q58=makeQuery(id+"F1.opExtrude","CAP_FACE",FACE,{"disambiguationData":[OSD([sQuery(id+"F0.wireOp",EDGE,"E1.bottom"),sQuery(id+"F0.wireOp",EDGE,"E1.top"),sQuery(id+"F0.wireOp",EDGE,"E1.left"),sQuery(id+"F0.wireOp",EDGE,"E1.right"),sQuery(id+"F0.wireOp",EDGE,"E3.trimOffspring"),sQuery(id+"F0.wireOp",EDGE,"E4.trimOffspring"),sQuery(id+"F0.wireOp",EDGE,"E54.trimOffspring"),sQuery(id+"F0.wireOp",EDGE,"E58"),sQuery(id+"F0.wireOp",EDGE,"E64")])],"isStart":true});
            var Q59;
            Q59=makeQuery(id+"F1.opExtrude","SWEPT_FACE",FACE,{"disambiguationData":[OSD([sQuery(id+"F0.wireOp",EDGE,"E1.top")])]});
            var Q60;
            Q60=makeQuery(id+"F1.opExtrude","CAP_FACE",FACE,{"disambiguationData":[OSD([sQuery(id+"F0.wireOp",EDGE,"E9.MirrorCS"),sQuery(id+"F0.wireOp",EDGE,"E15.MirrorCS"),sQuery(id+"F0.wireOp",EDGE,"E16.MirrorCS"),sQuery(id+"F0.wireOp",EDGE,"E17.MirrorCS"),sQuery(id+"F0.wireOp",EDGE,"E18.MirrorCS"),sQuery(id+"F0.wireOp",EDGE,"E20.MirrorCS"),sQuery(id+"F0.wireOp",EDGE,"E51.trimOffspring"),sQuery(id+"F0.wireOp",EDGE,"E59"),sQuery(id+"F0.wireOp",EDGE,"E68")])],"isStart":true});
            var Q61;
            Q61=makeQuery(id+"F1.opExtrude","CAP_FACE",FACE,{"disambiguationData":[OSD([sQuery(id+"F0.wireOp",EDGE,"E0.top"),sQuery(id+"F0.wireOp",EDGE,"E0.right"),sQuery(id+"F0.wireOp",EDGE,"E10.MirrorCS"),sQuery(id+"F0.wireOp",EDGE,"E11.MirrorCS"),sQuery(id+"F0.wireOp",EDGE,"E30.MirrorCS"),sQuery(id+"F0.wireOp",EDGE,"E31.MirrorCS"),sQuery(id+"F0.wireOp",EDGE,"E37.MirrorCS"),sQuery(id+"F0.wireOp",EDGE,"E40.MirrorCS"),sQuery(id+"F0.wireOp",EDGE,"E57"),sQuery(id+"F0.wireOp",EDGE,"E60"),sQuery(id+"F0.wireOp",EDGE,"E65"),sQuery(id+"F0.wireOp",EDGE,"E66")])],"isStart":true});
            var Q62;
            Q62=makeQuery(id+"F2.opExtrude","SWEPT_FACE",FACE,{"disambiguationData":[OSD([sQuery(id+"F0.wireOp",EDGE,"E59")])]});
            var Q63;
            Q63=makeQuery(id+"F2.opExtrude","SWEPT_FACE",FACE,{"disambiguationData":[OSD([sQuery(id+"F0.wireOp",EDGE,"E57")])]});
            var Q64;
            Q64=makeQuery(id+"F2.opExtrude","CAP_FACE",FACE,{"disambiguationData":[OSD([sQuery(id+"F0.wireOp",EDGE,"E2.bottom"),sQuery(id+"F0.wireOp",EDGE,"E2.top"),sQuery(id+"F0.wireOp",EDGE,"E5.right"),sQuery(id+"F0.wireOp",EDGE,"E14.MirrorCS"),sQuery(id+"F0.wireOp",EDGE,"E21.MirrorCS"),sQuery(id+"F0.wireOp",EDGE,"E22.MirrorCS"),sQuery(id+"F0.wireOp",EDGE,"E57"),sQuery(id+"F0.wireOp",EDGE,"E58"),sQuery(id+"F0.wireOp",EDGE,"E59")])],"isStart":true});
            var Q65;
            Q65=makeQuery(id+"F2.opExtrude","SWEPT_FACE",FACE,{"disambiguationData":[OSD([sQuery(id+"F0.wireOp",EDGE,"E58")])]});
            var Q66;
            Q66=makeQuery(id+"F2.opExtrude","SWEPT_FACE",FACE,{"disambiguationData":[OSD([sQuery(id+"F0.wireOp",EDGE,"E2.top"),sQuery(id+"F0.wireOp",EDGE,"E22.MirrorCS")])]});
            var Q67;
            Q67=makeQuery(id+"F2.opExtrude","SWEPT_FACE",FACE,{"disambiguationData":[OSD([sQuery(id+"F0.wireOp",EDGE,"E64")])]});
            var Q68;
            Q68=makeQuery(id+"F2.opExtrude","SWEPT_FACE",FACE,{"disambiguationData":[OSD([sQuery(id+"F0.wireOp",EDGE,"E63")])]});
            var Q69;
            Q69=makeQuery(id+"F2.opExtrude","SWEPT_FACE",FACE,{"disambiguationData":[OSD([sQuery(id+"F0.wireOp",EDGE,"E66")])]});
            var Q70;
            Q70=makeQuery(id+"F2.opExtrude","SWEPT_FACE",FACE,{"disambiguationData":[OSD([sQuery(id+"F0.wireOp",EDGE,"E68")])]});
            var Q71;
            Q71=makeQuery(id+"F2.opExtrude","CAP_FACE",FACE,{"disambiguationData":[OSD([sQuery(id+"F0.wireOp",EDGE,"E12.MirrorCS"),sQuery(id+"F0.wireOp",EDGE,"E13.MirrorCS"),sQuery(id+"F0.wireOp",EDGE,"E19.MirrorCS"),sQuery(id+"F0.wireOp",EDGE,"E33.MirrorCS"),sQuery(id+"F0.wireOp",EDGE,"E42.MirrorCS"),sQuery(id+"F0.wireOp",EDGE,"E44.MirrorCS"),sQuery(id+"F0.wireOp",EDGE,"E66"),sQuery(id+"F0.wireOp",EDGE,"E67"),sQuery(id+"F0.wireOp",EDGE,"E68")])],"isStart":true});
            var Q72;
            Q72=makeQuery(id+"F2.opExtrude","SWEPT_FACE",FACE,{"disambiguationData":[OSD([sQuery(id+"F0.wireOp",EDGE,"E67")])]});
            var Q73;
            Q73=makeQuery(id+"F2.opExtrude","SWEPT_FACE",FACE,{"disambiguationData":[OSD([sQuery(id+"F0.wireOp",EDGE,"E62")])]});
            var Q74;
            Q74=makeQuery(id+"F2.opExtrude","CAP_FACE",FACE,{"disambiguationData":[OSD([sQuery(id+"F0.wireOp",EDGE,"E28.MirrorCS"),sQuery(id+"F0.wireOp",EDGE,"E32.MirrorCS"),sQuery(id+"F0.wireOp",EDGE,"E34.MirrorCS"),sQuery(id+"F0.wireOp",EDGE,"E36.MirrorCS"),sQuery(id+"F0.wireOp",EDGE,"E45.MirrorCS"),sQuery(id+"F0.wireOp",EDGE,"E46.MirrorCS"),sQuery(id+"F0.wireOp",EDGE,"E55.top"),sQuery(id+"F0.wireOp",EDGE,"E55.left"),sQuery(id+"F0.wireOp",EDGE,"E55.right"),sQuery(id+"F0.wireOp",EDGE,"E60"),sQuery(id+"F0.wireOp",EDGE,"E61"),sQuery(id+"F0.wireOp",EDGE,"E62")])],"isStart":true});
            var Q75;
            Q75=makeQuery(id+"F2.opExtrude","SWEPT_FACE",FACE,{"disambiguationData":[OSD([sQuery(id+"F0.wireOp",EDGE,"E60")])]});
            var Q76;
            Q76=makeQuery(id+"F2.opExtrude","SWEPT_FACE",FACE,{"disambiguationData":[OSD([sQuery(id+"F0.wireOp",EDGE,"E45.MirrorCS")])]});
            var Q77;
            Q77=makeQuery(id+"F1.opExtrude","SWEPT_FACE",FACE,{"disambiguationData":[OSD([sQuery(id+"F0.wireOp",EDGE,"E49.MirrorCS")])]});
            var Q78;
            Q78=makeQuery(id+"F1.opExtrude","SWEPT_BODY",BODY,{"disambiguationData":[OSD([sQuery(id+"F0.wireOp",EDGE,"E0.top"),sQuery(id+"F0.wireOp",EDGE,"E0.right"),sQuery(id+"F0.wireOp",EDGE,"E10.MirrorCS"),sQuery(id+"F0.wireOp",EDGE,"E11.MirrorCS"),sQuery(id+"F0.wireOp",EDGE,"E30.MirrorCS"),sQuery(id+"F0.wireOp",EDGE,"E31.MirrorCS"),sQuery(id+"F0.wireOp",EDGE,"E37.MirrorCS"),sQuery(id+"F0.wireOp",EDGE,"E40.MirrorCS"),sQuery(id+"F0.wireOp",EDGE,"E57"),sQuery(id+"F0.wireOp",EDGE,"E60"),sQuery(id+"F0.wireOp",EDGE,"E65"),sQuery(id+"F0.wireOp",EDGE,"E66")])]});
            var Q79;
            Q79=makeQuery(id+"F2.opExtrude","SWEPT_BODY",BODY,{"disambiguationData":[OSD([sQuery(id+"F0.wireOp",EDGE,"E12.MirrorCS"),sQuery(id+"F0.wireOp",EDGE,"E13.MirrorCS"),sQuery(id+"F0.wireOp",EDGE,"E19.MirrorCS"),sQuery(id+"F0.wireOp",EDGE,"E33.MirrorCS"),sQuery(id+"F0.wireOp",EDGE,"E42.MirrorCS"),sQuery(id+"F0.wireOp",EDGE,"E44.MirrorCS"),sQuery(id+"F0.wireOp",EDGE,"E66"),sQuery(id+"F0.wireOp",EDGE,"E67"),sQuery(id+"F0.wireOp",EDGE,"E68")])]});
            var Q80;
            Q80=makeQuery(id+"F1.opExtrude","SWEPT_BODY",BODY,{"disambiguationData":[OSD([sQuery(id+"F0.wireOp",EDGE,"E9.MirrorCS"),sQuery(id+"F0.wireOp",EDGE,"E15.MirrorCS"),sQuery(id+"F0.wireOp",EDGE,"E16.MirrorCS"),sQuery(id+"F0.wireOp",EDGE,"E17.MirrorCS"),sQuery(id+"F0.wireOp",EDGE,"E18.MirrorCS"),sQuery(id+"F0.wireOp",EDGE,"E20.MirrorCS"),sQuery(id+"F0.wireOp",EDGE,"E51.trimOffspring"),sQuery(id+"F0.wireOp",EDGE,"E59"),sQuery(id+"F0.wireOp",EDGE,"E68")])]});
            var Q81;
            Q81=makeQuery(id+"F2.opExtrude","SWEPT_BODY",BODY,{"disambiguationData":[OSD([sQuery(id+"F0.wireOp",EDGE,"E2.bottom"),sQuery(id+"F0.wireOp",EDGE,"E2.top"),sQuery(id+"F0.wireOp",EDGE,"E5.right"),sQuery(id+"F0.wireOp",EDGE,"E14.MirrorCS"),sQuery(id+"F0.wireOp",EDGE,"E21.MirrorCS"),sQuery(id+"F0.wireOp",EDGE,"E22.MirrorCS"),sQuery(id+"F0.wireOp",EDGE,"E57"),sQuery(id+"F0.wireOp",EDGE,"E58"),sQuery(id+"F0.wireOp",EDGE,"E59")])]});
            var Q82;
            Q82=makeQuery(id+"F1.opExtrude","SWEPT_BODY",BODY,{"disambiguationData":[OSD([sQuery(id+"F0.wireOp",EDGE,"E1.bottom"),sQuery(id+"F0.wireOp",EDGE,"E1.top"),sQuery(id+"F0.wireOp",EDGE,"E1.left"),sQuery(id+"F0.wireOp",EDGE,"E1.right"),sQuery(id+"F0.wireOp",EDGE,"E3.trimOffspring"),sQuery(id+"F0.wireOp",EDGE,"E4.trimOffspring"),sQuery(id+"F0.wireOp",EDGE,"E54.trimOffspring"),sQuery(id+"F0.wireOp",EDGE,"E58"),sQuery(id+"F0.wireOp",EDGE,"E64")])]});
            var Q83;
            Q83=makeQuery(id+"F2.opExtrude","SWEPT_BODY",BODY,{"disambiguationData":[OSD([sQuery(id+"F0.wireOp",EDGE,"E6.left"),sQuery(id+"F0.wireOp",EDGE,"E7.top"),sQuery(id+"F0.wireOp",EDGE,"E8"),sQuery(id+"F0.wireOp",EDGE,"E38.MirrorCS"),sQuery(id+"F0.wireOp",EDGE,"E41.MirrorCS"),sQuery(id+"F0.wireOp",EDGE,"E49.MirrorCS"),sQuery(id+"F0.wireOp",EDGE,"E63"),sQuery(id+"F0.wireOp",EDGE,"E64"),sQuery(id+"F0.wireOp",EDGE,"E65")])]});
            var Q84;
            Q84=makeQuery(id+"F1.opExtrude","SWEPT_BODY",BODY,{"disambiguationData":[OSD([sQuery(id+"F0.wireOp",EDGE,"E25.MirrorCS"),sQuery(id+"F0.wireOp",EDGE,"E26.MirrorCS"),sQuery(id+"F0.wireOp",EDGE,"E29.MirrorCS"),sQuery(id+"F0.wireOp",EDGE,"E39.MirrorCS"),sQuery(id+"F0.wireOp",EDGE,"E41.MirrorCS"),sQuery(id+"F0.wireOp",EDGE,"E47.MirrorCS"),sQuery(id+"F0.wireOp",EDGE,"E48.MirrorCS"),sQuery(id+"F0.wireOp",EDGE,"E49.MirrorCS"),sQuery(id+"F0.wireOp",EDGE,"E53.trimOffspring"),sQuery(id+"F0.wireOp",EDGE,"E62"),sQuery(id+"F0.wireOp",EDGE,"E63")])]});
            var Q85;
            Q85=makeQuery(id+"F2.opExtrude","SWEPT_BODY",BODY,{"disambiguationData":[OSD([sQuery(id+"F0.wireOp",EDGE,"E28.MirrorCS"),sQuery(id+"F0.wireOp",EDGE,"E32.MirrorCS"),sQuery(id+"F0.wireOp",EDGE,"E34.MirrorCS"),sQuery(id+"F0.wireOp",EDGE,"E36.MirrorCS"),sQuery(id+"F0.wireOp",EDGE,"E45.MirrorCS"),sQuery(id+"F0.wireOp",EDGE,"E46.MirrorCS"),sQuery(id+"F0.wireOp",EDGE,"E55.top"),sQuery(id+"F0.wireOp",EDGE,"E55.left"),sQuery(id+"F0.wireOp",EDGE,"E55.right"),sQuery(id+"F0.wireOp",EDGE,"E60"),sQuery(id+"F0.wireOp",EDGE,"E61"),sQuery(id+"F0.wireOp",EDGE,"E62")])]});
            var Q86;
            Q86=makeQuery(id+"F1.opExtrude","SWEPT_BODY",BODY,{"disambiguationData":[OSD([sQuery(id+"F0.wireOp",EDGE,"E23.MirrorCS"),sQuery(id+"F0.wireOp",EDGE,"E24.MirrorCS"),sQuery(id+"F0.wireOp",EDGE,"E27.MirrorCS"),sQuery(id+"F0.wireOp",EDGE,"E35.MirrorCS"),sQuery(id+"F0.wireOp",EDGE,"E43.MirrorCS"),sQuery(id+"F0.wireOp",EDGE,"E50.MirrorCS"),sQuery(id+"F0.wireOp",EDGE,"E52.trimOffspring"),sQuery(id+"F0.wireOp",EDGE,"E61"),sQuery(id+"F0.wireOp",EDGE,"E67")])]});
            shell(context, id + "F4", {"isHollow" : true, "entities" : qUnion([Q0, Q1, Q2, Q3, Q4, Q5, Q6, Q7, Q8, Q9, Q10, Q11, Q12, Q13, Q14, Q15, Q16, Q17, Q18, Q19, Q20, Q21, Q22, Q23, Q24, Q25, Q26, Q27, Q28, Q29, Q30, Q31, Q32, Q33, Q34, Q35, Q36, Q37, Q38, Q39, Q40, Q41, Q42, Q43, Q44, Q45, Q46, Q47, Q48, Q49, Q50, Q51, Q52, Q53, Q54, Q55, Q56, Q57, Q58, Q59, Q60, Q61, Q62, Q63, Q64, Q65, Q66, Q67, Q68, Q69, Q70, Q71, Q72, Q73, Q74, Q75, Q76, Q77]), "parts" : qUnion([Q78, Q79, Q80, Q81, Q82, Q83, Q84, Q85, Q86]), "thickness" : 25.4 * mm});
        }
        {
            var Q0;
            Q0=makeQuery(id+"F2.opExtrude","SWEPT_FACE",FACE,{"disambiguationData":[OSD([sQuery(id+"F0.wireOp",EDGE,"E55.top")])]});
            var sketch = newSketch(context, id + "F5", { "sketchPlane" : qUnion([Q0])});
            skLineSegment(sketch, "E69.bottom", {"start": v(-1455.23, 102.64) * mm, "end": v(1455.23, 102.64) * mm});
            skLineSegment(sketch, "E69.top", {"start": v(-1455.23, 2046.79) * mm, "end": v(1455.23, 2046.79) * mm});
            skLineSegment(sketch, "E69.left", {"start": v(-1455.23, 102.64) * mm, "end": v(-1455.23, 2046.79) * mm});
            skLineSegment(sketch, "E69.right", {"start": v(1455.23, 102.64) * mm, "end": v(1455.23, 2046.79) * mm});
            skSolve(sketch);
        }
        {
            var Q0;
            Q0=makeQuery(id+"F5.imprint","IMPRINT",FACE,{"disambiguationData":[TD([[makeQuery(id+"F5.imprint","IMPRINT",EDGE,{"derivedFrom":sQuery(id+"F5.wireOp",EDGE,"E69.bottom")}),1.0]])]});
            extrude(context, id + "F6", {"entities" : qUnion([Q0]), "operationType" : NewBodyOperationType.REMOVE, "oppositeDirection" : true, "depth" : 25.4 * mm, "offsetDistance" : 25.4 * mm});
        }
    });
